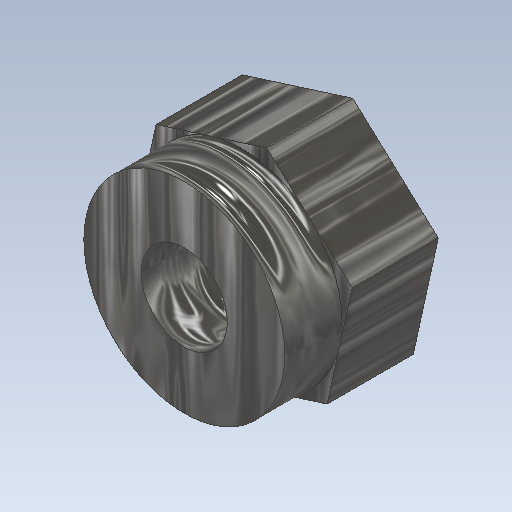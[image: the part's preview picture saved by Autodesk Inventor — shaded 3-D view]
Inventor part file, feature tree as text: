
AUTODESK INVENTOR PART (.ipt)
format: ipt  version: 2020.2 (Build 242310000, 310)  size: 222,720 bytes
history: native  units: mm
features: extrude x2, hole x2, other x1, sketch x1
ambient origin geometry x8: Origin, YZ Plane, XZ Plane, XY Plane, X Axis, Y Axis, Z Axis, Center Point
bodies: Body1 (feature_tree)
feature tree (6):
  other  "ソリッド1"
  sketch  "スケッチ1"
  extrude  "押し出し1"  Depth=8.082904mm
  extrude  "押し出し2"  Depth=7.0mm
  hole  "穴1"  [1 undecoded]
  hole  "穴2"  [1 undecoded]
note: 2 required parameter values undecoded (feature->parameter linkage not recoverable at this tier; creation-order binding heuristic only, values carry confidence <= 0.55)
